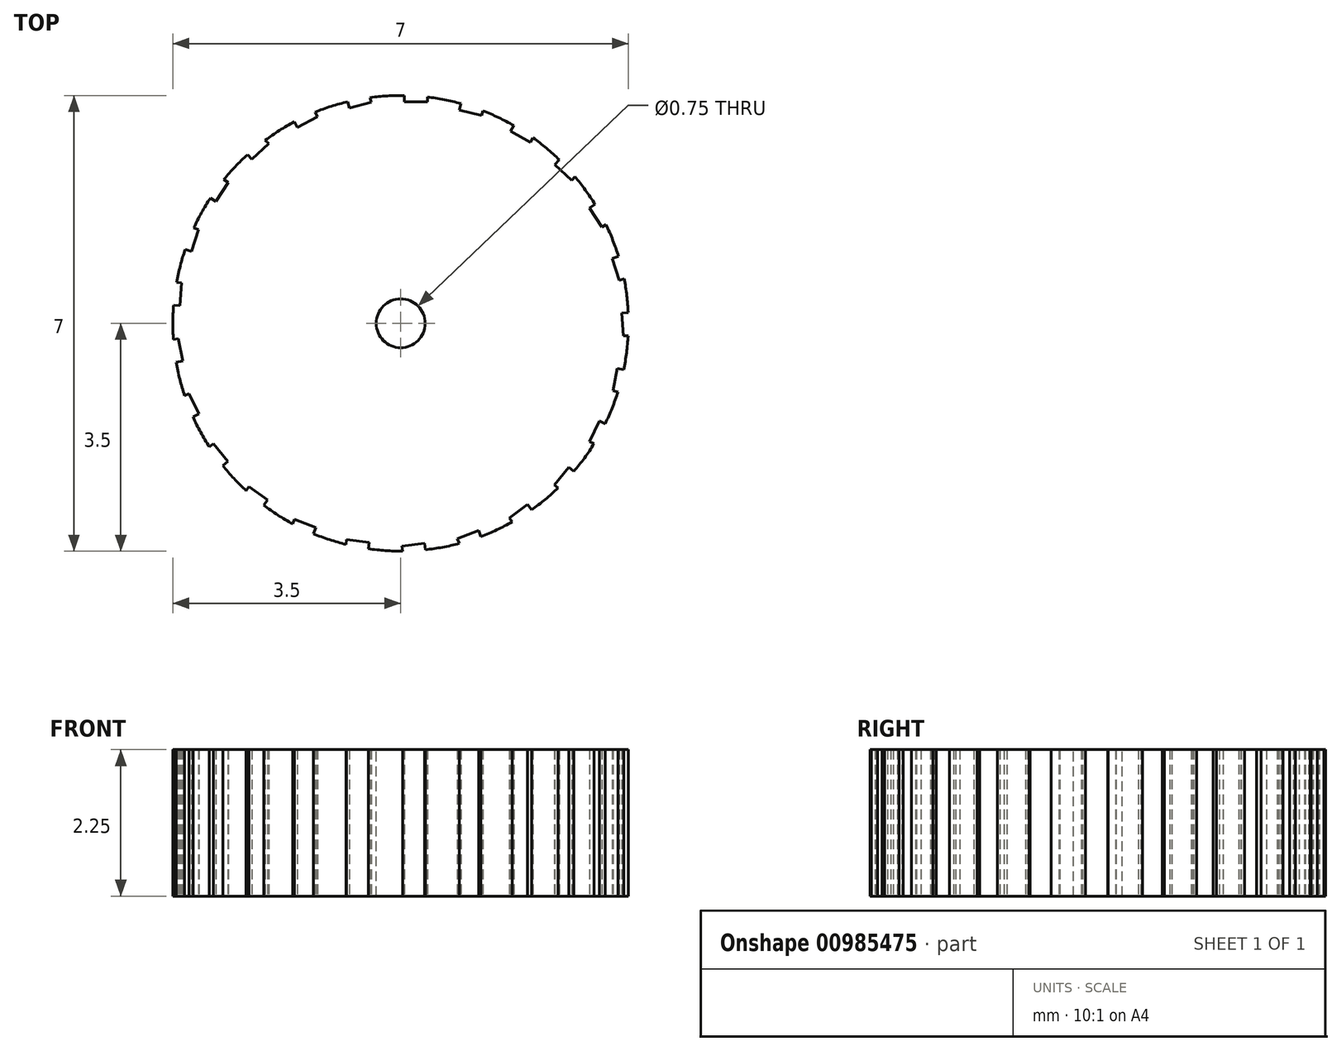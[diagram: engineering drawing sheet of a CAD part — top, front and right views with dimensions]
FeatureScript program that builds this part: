
annotation { "Feature Type Name" : "Feature", "Feature Type Description" : "" }
export const myFeature = defineFeature(function(context is Context, id is Id, definition is map)
    precondition{}
    {
        {
            var Q0;
            Q0=qCreatedBy(makeId("Top.planeOp"),FACE);
            var sketch = newSketch(context, id + "F0", { "sketchPlane" : qUnion([Q0])});
            skCircle(sketch, "E0", {"center": v(0, 0) * mm, "radius": 3.5 * mm});
            skLineSegment(sketch, "E1", {"start": v(0.06, 3.5) * mm, "end": v(0.06, 3.4) * mm});
            skLineSegment(sketch, "E2", {"start": v(0.06, 3.4) * mm, "end": v(0.4, 3.4) * mm});
            skLineSegment(sketch, "E3", {"start": v(0.4, 3.4) * mm, "end": v(0.4, 3.48) * mm});
            skArc(sketch, "E4", {"start": v(0.06, 3.5) * mm, "mid": v(0.23, 3.5) * mm, "end": v(0.4, 3.48) * mm});
            skLineSegment(sketch, "E5.1.0", {"start": v(-0.79, 3.3) * mm, "end": v(-0.45, 3.4) * mm});
            skLineSegment(sketch, "E5.1.1", {"start": v(-0.81, 3.4) * mm, "end": v(-0.79, 3.3) * mm});
            skArc(sketch, "E5.1.2", {"start": v(-0.81, 3.4) * mm, "mid": v(-0.64, 3.44) * mm, "end": v(-0.47, 3.47) * mm});
            skLineSegment(sketch, "E5.1.3", {"start": v(-0.45, 3.4) * mm, "end": v(-0.47, 3.47) * mm});
            skLineSegment(sketch, "E5.2.0", {"start": v(-1.59, 3) * mm, "end": v(-1.28, 3.18) * mm});
            skLineSegment(sketch, "E5.2.1", {"start": v(-1.63, 3.1) * mm, "end": v(-1.59, 3) * mm});
            skArc(sketch, "E5.2.2", {"start": v(-1.63, 3.1) * mm, "mid": v(-1.48, 3.17) * mm, "end": v(-1.32, 3.24) * mm});
            skLineSegment(sketch, "E5.2.3", {"start": v(-1.28, 3.18) * mm, "end": v(-1.32, 3.24) * mm});
            skLineSegment(sketch, "E5.3.0", {"start": v(-2.28, 2.52) * mm, "end": v(-2.03, 2.76) * mm});
            skLineSegment(sketch, "E5.3.1", {"start": v(-2.35, 2.6) * mm, "end": v(-2.28, 2.52) * mm});
            skArc(sketch, "E5.3.2", {"start": v(-2.35, 2.6) * mm, "mid": v(-2.22, 2.7) * mm, "end": v(-2.08, 2.81) * mm});
            skLineSegment(sketch, "E5.3.3", {"start": v(-2.03, 2.76) * mm, "end": v(-2.08, 2.81) * mm});
            skLineSegment(sketch, "E5.4.0", {"start": v(-2.84, 1.87) * mm, "end": v(-2.65, 2.17) * mm});
            skLineSegment(sketch, "E5.4.1", {"start": v(-2.92, 1.92) * mm, "end": v(-2.84, 1.87) * mm});
            skArc(sketch, "E5.4.2", {"start": v(-2.92, 1.92) * mm, "mid": v(-2.82, 2.07) * mm, "end": v(-2.72, 2.2) * mm});
            skLineSegment(sketch, "E5.4.3", {"start": v(-2.65, 2.17) * mm, "end": v(-2.72, 2.2) * mm});
            skLineSegment(sketch, "E5.5.0", {"start": v(-3.22, 1.1) * mm, "end": v(-3.1, 1.44) * mm});
            skLineSegment(sketch, "E5.5.1", {"start": v(-3.31, 1.14) * mm, "end": v(-3.22, 1.1) * mm});
            skArc(sketch, "E5.5.2", {"start": v(-3.31, 1.14) * mm, "mid": v(-3.25, 1.3) * mm, "end": v(-3.18, 1.46) * mm});
            skLineSegment(sketch, "E5.5.3", {"start": v(-3.1, 1.44) * mm, "end": v(-3.18, 1.46) * mm});
            skLineSegment(sketch, "E5.6.0", {"start": v(-3.39, 0.27) * mm, "end": v(-3.37, 0.62) * mm});
            skLineSegment(sketch, "E5.6.1", {"start": v(-3.49, 0.28) * mm, "end": v(-3.39, 0.27) * mm});
            skArc(sketch, "E5.6.2", {"start": v(-3.49, 0.28) * mm, "mid": v(-3.47, 0.45) * mm, "end": v(-3.44, 0.63) * mm});
            skLineSegment(sketch, "E5.6.3", {"start": v(-3.37, 0.62) * mm, "end": v(-3.44, 0.63) * mm});
            skLineSegment(sketch, "E5.7.0", {"start": v(-3.35, -0.58) * mm, "end": v(-3.42, -0.24) * mm});
            skLineSegment(sketch, "E5.7.1", {"start": v(-3.45, -0.6) * mm, "end": v(-3.35, -0.58) * mm});
            skArc(sketch, "E5.7.2", {"start": v(-3.45, -0.6) * mm, "mid": v(-3.47, -0.42) * mm, "end": v(-3.5, -0.25) * mm});
            skLineSegment(sketch, "E5.7.3", {"start": v(-3.42, -0.24) * mm, "end": v(-3.5, -0.25) * mm});
            skLineSegment(sketch, "E5.8.0", {"start": v(-3.1, -1.4) * mm, "end": v(-3.25, -1.08) * mm});
            skLineSegment(sketch, "E5.8.1", {"start": v(-3.2, -1.44) * mm, "end": v(-3.1, -1.4) * mm});
            skArc(sketch, "E5.8.2", {"start": v(-3.2, -1.44) * mm, "mid": v(-3.26, -1.28) * mm, "end": v(-3.32, -1.11) * mm});
            skLineSegment(sketch, "E5.8.3", {"start": v(-3.25, -1.08) * mm, "end": v(-3.32, -1.11) * mm});
            skLineSegment(sketch, "E5.9.0", {"start": v(-2.66, -2.12) * mm, "end": v(-2.88, -1.85) * mm});
            skLineSegment(sketch, "E5.9.1", {"start": v(-2.73, -2.19) * mm, "end": v(-2.66, -2.12) * mm});
            skArc(sketch, "E5.9.2", {"start": v(-2.73, -2.19) * mm, "mid": v(-2.84, -2.05) * mm, "end": v(-2.94, -1.9) * mm});
            skLineSegment(sketch, "E5.9.3", {"start": v(-2.88, -1.85) * mm, "end": v(-2.94, -1.9) * mm});
            skLineSegment(sketch, "E6.1.10.0", {"start": v(-2.05, -2.72) * mm, "end": v(-2.33, -2.51) * mm});
            skLineSegment(sketch, "E6.3.10.0", {"start": v(-2.1, -2.8) * mm, "end": v(-2.05, -2.72) * mm});
            skArc(sketch, "E6.6.10.0", {"start": v(-2.1, -2.8) * mm, "mid": v(-2.24, -2.69) * mm, "end": v(-2.37, -2.57) * mm});
            skLineSegment(sketch, "E6.10.10.0", {"start": v(-2.33, -2.51) * mm, "end": v(-2.37, -2.57) * mm});
            skLineSegment(sketch, "E6.1.11.0", {"start": v(-1.3, -3.14) * mm, "end": v(-1.63, -3.01) * mm});
            skLineSegment(sketch, "E6.3.11.0", {"start": v(-1.34, -3.23) * mm, "end": v(-1.3, -3.14) * mm});
            skArc(sketch, "E6.6.11.0", {"start": v(-1.34, -3.23) * mm, "mid": v(-1.5, -3.16) * mm, "end": v(-1.66, -3.08) * mm});
            skLineSegment(sketch, "E6.10.11.0", {"start": v(-1.63, -3.01) * mm, "end": v(-1.66, -3.08) * mm});
            skLineSegment(sketch, "E6.1.12.0", {"start": v(-0.48, -3.37) * mm, "end": v(-0.83, -3.32) * mm});
            skLineSegment(sketch, "E6.3.12.0", {"start": v(-0.5, -3.46) * mm, "end": v(-0.48, -3.37) * mm});
            skArc(sketch, "E6.6.12.0", {"start": v(-0.5, -3.46) * mm, "mid": v(-0.67, -3.44) * mm, "end": v(-0.84, -3.4) * mm});
            skLineSegment(sketch, "E6.10.12.0", {"start": v(-0.83, -3.32) * mm, "end": v(-0.84, -3.4) * mm});
            skLineSegment(sketch, "E6.1.13.0", {"start": v(0.37, -3.38) * mm, "end": v(0.02, -3.42) * mm});
            skLineSegment(sketch, "E6.3.13.0", {"start": v(0.38, -3.48) * mm, "end": v(0.37, -3.38) * mm});
            skArc(sketch, "E6.6.13.0", {"start": v(0.38, -3.48) * mm, "mid": v(0.2, -3.5) * mm, "end": v(0.03, -3.5) * mm});
            skLineSegment(sketch, "E6.10.13.0", {"start": v(0.02, -3.42) * mm, "end": v(0.03, -3.5) * mm});
            skLineSegment(sketch, "E7.1.14.0", {"start": v(1.2, -3.18) * mm, "end": v(0.87, -3.31) * mm});
            skLineSegment(sketch, "E7.3.14.0", {"start": v(1.23, -3.28) * mm, "end": v(1.2, -3.18) * mm});
            skArc(sketch, "E7.6.14.0", {"start": v(1.23, -3.28) * mm, "mid": v(1.07, -3.33) * mm, "end": v(0.9, -3.38) * mm});
            skLineSegment(sketch, "E7.10.14.0", {"start": v(0.87, -3.31) * mm, "end": v(0.9, -3.38) * mm});
            skLineSegment(sketch, "E7.1.15.0", {"start": v(1.95, -2.78) * mm, "end": v(1.67, -3) * mm});
            skLineSegment(sketch, "E7.3.15.0", {"start": v(2, -2.87) * mm, "end": v(1.95, -2.78) * mm});
            skArc(sketch, "E7.6.15.0", {"start": v(2, -2.87) * mm, "mid": v(1.86, -2.96) * mm, "end": v(1.71, -3.05) * mm});
            skLineSegment(sketch, "E7.10.15.0", {"start": v(1.67, -3) * mm, "end": v(1.71, -3.05) * mm});
            skLineSegment(sketch, "E7.1.16.0", {"start": v(2.58, -2.21) * mm, "end": v(2.36, -2.48) * mm});
            skLineSegment(sketch, "E7.3.16.0", {"start": v(2.66, -2.28) * mm, "end": v(2.58, -2.21) * mm});
            skArc(sketch, "E7.6.16.0", {"start": v(2.66, -2.28) * mm, "mid": v(2.54, -2.4) * mm, "end": v(2.42, -2.53) * mm});
            skLineSegment(sketch, "E7.10.16.0", {"start": v(2.36, -2.48) * mm, "end": v(2.42, -2.53) * mm});
            skLineSegment(sketch, "E7.1.17.0", {"start": v(3.05, -1.5) * mm, "end": v(2.9, -1.82) * mm});
            skLineSegment(sketch, "E7.3.17.0", {"start": v(3.14, -1.54) * mm, "end": v(3.05, -1.5) * mm});
            skArc(sketch, "E7.6.17.0", {"start": v(3.14, -1.54) * mm, "mid": v(3.06, -1.7) * mm, "end": v(2.97, -1.85) * mm});
            skLineSegment(sketch, "E7.10.17.0", {"start": v(2.9, -1.82) * mm, "end": v(2.97, -1.85) * mm});
            skLineSegment(sketch, "E7.1.18.0", {"start": v(3.33, -0.7) * mm, "end": v(3.26, -1.04) * mm});
            skLineSegment(sketch, "E7.3.18.0", {"start": v(3.43, -0.71) * mm, "end": v(3.33, -0.7) * mm});
            skArc(sketch, "E7.6.18.0", {"start": v(3.43, -0.71) * mm, "mid": v(3.39, -0.88) * mm, "end": v(3.34, -1.05) * mm});
            skLineSegment(sketch, "E7.10.18.0", {"start": v(3.26, -1.04) * mm, "end": v(3.34, -1.05) * mm});
            skLineSegment(sketch, "E7.1.19.0", {"start": v(3.4, 0.15) * mm, "end": v(3.42, -0.2) * mm});
            skLineSegment(sketch, "E7.3.19.0", {"start": v(3.5, 0.16) * mm, "end": v(3.4, 0.15) * mm});
            skArc(sketch, "E7.6.19.0", {"start": v(3.5, 0.16) * mm, "mid": v(3.5, -0.01) * mm, "end": v(3.5, -0.19) * mm});
            skLineSegment(sketch, "E7.10.19.0", {"start": v(3.42, -0.2) * mm, "end": v(3.5, -0.19) * mm});
            skLineSegment(sketch, "E8.1.20.0", {"start": v(3.25, 1) * mm, "end": v(3.36, 0.66) * mm});
            skLineSegment(sketch, "E8.3.20.0", {"start": v(3.35, 1.03) * mm, "end": v(3.25, 1) * mm});
            skArc(sketch, "E8.6.20.0", {"start": v(3.35, 1.03) * mm, "mid": v(3.4, 0.86) * mm, "end": v(3.43, 0.69) * mm});
            skLineSegment(sketch, "E8.10.20.0", {"start": v(3.36, 0.66) * mm, "end": v(3.43, 0.69) * mm});
            skLineSegment(sketch, "E8.1.21.0", {"start": v(2.9, 1.77) * mm, "end": v(3.09, 1.48) * mm});
            skLineSegment(sketch, "E8.3.21.0", {"start": v(2.99, 1.83) * mm, "end": v(2.9, 1.77) * mm});
            skArc(sketch, "E8.6.21.0", {"start": v(2.99, 1.83) * mm, "mid": v(3.07, 1.67) * mm, "end": v(3.15, 1.52) * mm});
            skLineSegment(sketch, "E8.10.21.0", {"start": v(3.09, 1.48) * mm, "end": v(3.15, 1.52) * mm});
            skLineSegment(sketch, "E8.1.22.0", {"start": v(2.37, 2.44) * mm, "end": v(2.62, 2.2) * mm});
            skLineSegment(sketch, "E8.3.22.0", {"start": v(2.44, 2.51) * mm, "end": v(2.37, 2.44) * mm});
            skArc(sketch, "E8.6.22.0", {"start": v(2.44, 2.51) * mm, "mid": v(2.56, 2.39) * mm, "end": v(2.68, 2.25) * mm});
            skLineSegment(sketch, "E8.10.22.0", {"start": v(2.62, 2.2) * mm, "end": v(2.68, 2.25) * mm});
            skLineSegment(sketch, "E8.1.23.0", {"start": v(1.69, 2.95) * mm, "end": v(2, 2.78) * mm});
            skLineSegment(sketch, "E8.3.23.0", {"start": v(1.74, 3.04) * mm, "end": v(1.69, 2.95) * mm});
            skArc(sketch, "E8.6.23.0", {"start": v(1.74, 3.04) * mm, "mid": v(1.89, 2.95) * mm, "end": v(2.03, 2.85) * mm});
            skLineSegment(sketch, "E8.10.23.0", {"start": v(2, 2.78) * mm, "end": v(2.03, 2.85) * mm});
            skLineSegment(sketch, "E8.1.24.0", {"start": v(0.9, 3.28) * mm, "end": v(1.24, 3.2) * mm});
            skLineSegment(sketch, "E8.3.24.0", {"start": v(0.93, 3.37) * mm, "end": v(0.9, 3.28) * mm});
            skArc(sketch, "E8.6.24.0", {"start": v(0.93, 3.37) * mm, "mid": v(1.1, 3.32) * mm, "end": v(1.26, 3.27) * mm});
            skLineSegment(sketch, "E8.10.24.0", {"start": v(1.24, 3.2) * mm, "end": v(1.26, 3.27) * mm});
            skSolve(sketch);
        }
        {
            var Q0;
            {var subQ24=sQuery(id+"F0.wireOp",EDGE,"E1");Q0=makeQuery(id+"F0.imprint","IMPRINT",FACE,{"disambiguationData":[TD([[makeQuery(id+"F0.imprint","IMPRINT",EDGE,{"derivedFrom":subQ24}),-1.0]])]});}
            extrude(context, id + "F1", {"entities" : qUnion([Q0]), "depth" : 2.25 * mm});
        }
        {
            var Q0;
            Q0=makeQuery(id+"F1.opExtrude","CAP_FACE",FACE,{"disambiguationData":[OSD([sQuery(id+"F0.wireOp",EDGE,"E0"),sQuery(id+"F0.wireOp",EDGE,"E1"),sQuery(id+"F0.wireOp",EDGE,"E2"),sQuery(id+"F0.wireOp",EDGE,"E3"),sQuery(id+"F0.wireOp",EDGE,"E5.1.0"),sQuery(id+"F0.wireOp",EDGE,"E5.1.1"),sQuery(id+"F0.wireOp",EDGE,"E5.1.3"),sQuery(id+"F0.wireOp",EDGE,"E5.2.0"),sQuery(id+"F0.wireOp",EDGE,"E5.2.1"),sQuery(id+"F0.wireOp",EDGE,"E5.2.3"),sQuery(id+"F0.wireOp",EDGE,"E5.3.0"),sQuery(id+"F0.wireOp",EDGE,"E5.3.1"),sQuery(id+"F0.wireOp",EDGE,"E5.3.3"),sQuery(id+"F0.wireOp",EDGE,"E5.4.0"),sQuery(id+"F0.wireOp",EDGE,"E5.4.1"),sQuery(id+"F0.wireOp",EDGE,"E5.4.3"),sQuery(id+"F0.wireOp",EDGE,"E5.5.0"),sQuery(id+"F0.wireOp",EDGE,"E5.5.1"),sQuery(id+"F0.wireOp",EDGE,"E5.5.3"),sQuery(id+"F0.wireOp",EDGE,"E5.6.0"),sQuery(id+"F0.wireOp",EDGE,"E5.6.1"),sQuery(id+"F0.wireOp",EDGE,"E5.6.3"),sQuery(id+"F0.wireOp",EDGE,"E5.7.0"),sQuery(id+"F0.wireOp",EDGE,"E5.7.1"),sQuery(id+"F0.wireOp",EDGE,"E5.7.3"),sQuery(id+"F0.wireOp",EDGE,"E5.8.0"),sQuery(id+"F0.wireOp",EDGE,"E5.8.1"),sQuery(id+"F0.wireOp",EDGE,"E5.8.3"),sQuery(id+"F0.wireOp",EDGE,"E5.9.0"),sQuery(id+"F0.wireOp",EDGE,"E5.9.1"),sQuery(id+"F0.wireOp",EDGE,"E5.9.3"),sQuery(id+"F0.wireOp",EDGE,"E6.1.10.0"),sQuery(id+"F0.wireOp",EDGE,"E6.3.10.0"),sQuery(id+"F0.wireOp",EDGE,"E6.10.10.0"),sQuery(id+"F0.wireOp",EDGE,"E6.1.11.0"),sQuery(id+"F0.wireOp",EDGE,"E6.3.11.0"),sQuery(id+"F0.wireOp",EDGE,"E6.10.11.0"),sQuery(id+"F0.wireOp",EDGE,"E6.1.12.0"),sQuery(id+"F0.wireOp",EDGE,"E6.3.12.0"),sQuery(id+"F0.wireOp",EDGE,"E6.10.12.0"),sQuery(id+"F0.wireOp",EDGE,"E6.1.13.0"),sQuery(id+"F0.wireOp",EDGE,"E6.3.13.0"),sQuery(id+"F0.wireOp",EDGE,"E6.10.13.0")])],"isStart":false});
            var sketch = newSketch(context, id + "F2", { "sketchPlane" : qUnion([Q0])});
            skCircle(sketch, "E9", {"center": v(0, 0) * mm, "radius": 0.37 * mm});
            skSolve(sketch);
        }
        {
            var Q0;
            Q0=qSketchRegion(id+"F2",true);
            extrude(context, id + "F3", {"entities" : qUnion([Q0]), "operationType" : NewBodyOperationType.REMOVE, "endBound" : BoundingType.THROUGH_ALL, "oppositeDirection" : true, "depth" : 25 * mm});
        }
    });
